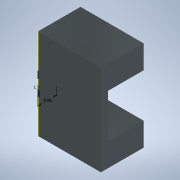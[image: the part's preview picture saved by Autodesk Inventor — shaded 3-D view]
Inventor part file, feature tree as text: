
AUTODESK INVENTOR PART (.ipt)
format: ipt  version: 2022 (Build 260153000, 153)  size: 175,616 bytes
history: native  units: mm
features: other x5, extrude x4, sketch x4, reference x4
ambient origin geometry x8: Origin, YZ Plane, XZ Plane, XY Plane, X Axis, Y Axis, Z Axis, Center Point
bodies: Solid1 (feature_tree)
feature tree (17):
  extrude  "Extrusion1"  Depth=0.3mm
  extrude  "Extrusion3"  Depth=0.3mm
  sketch  "Sketch5"  dims[d4=0.3mm d5=24.4mm]
  extrude  "Extrusion4"  Depth=24.4mm
  extrude  "Extrusion5"  Depth=3.0mm
  sketch  "Sketch16"  dims[d6=3.8mm d7=3.0mm d8=15.0mm d9=0.0mm d12=3.0mm d13=0.0mm d14=4.0mm d15=6.0mm d16=8.0mm d17=9.2mm d18=1.0mm d19=0.0mm d20=80.0mm d21=0.0mm d41=3.0mm d42=1.9mm d43=8.06mm d36=0.5mm d37=0.872665mm d38=0.5mm d39=0.872665mm]
  sketch  "Sketch1"  dims[d0=0.3mm d1=0.3mm]
  reference  "Reference1"
  reference  "Reference2"
  reference  "Reference3"
  reference  "Reference4"
  sketch  "Sketch4"  dims[d2=0.3mm d3=0.3mm]
  other  "<userpath>\OneDrive\Escritorio\Mini_Proyecto_Diseno\Diseno_18012\Modelo_MPD\Carril.iam"
  other  "Carril.iam"
  other  "Lateral_Carril:2"
  other  "Lateral_Carril:1"
  other  "Base_Carril:1"
